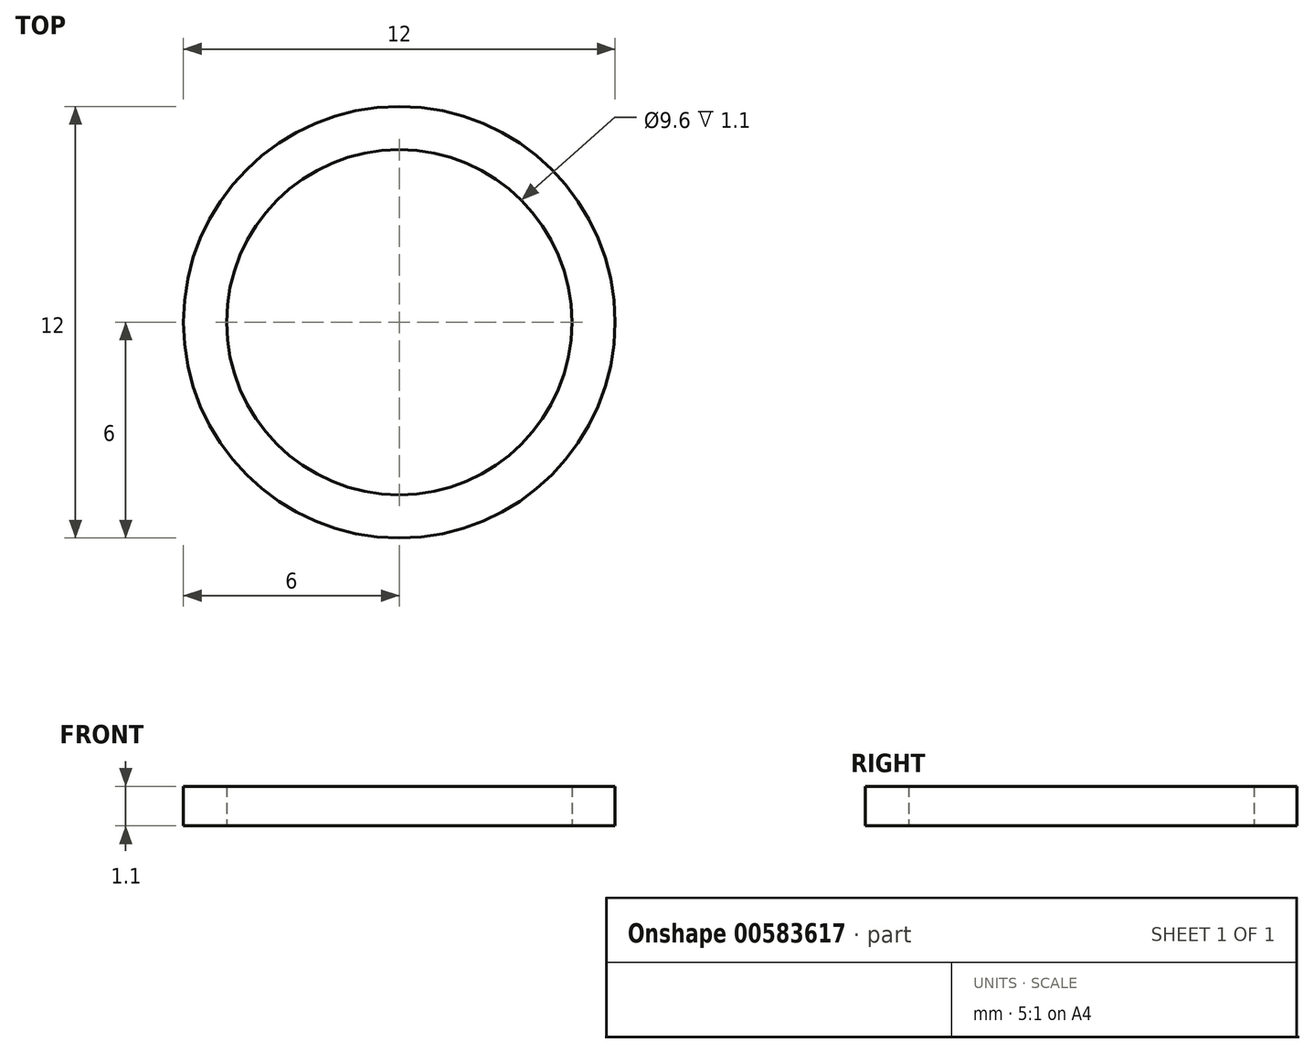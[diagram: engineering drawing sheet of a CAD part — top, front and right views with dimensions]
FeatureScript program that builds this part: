
annotation { "Feature Type Name" : "Feature", "Feature Type Description" : "" }
export const myFeature = defineFeature(function(context is Context, id is Id, definition is map)
    precondition{}
    {
        {
            var Q0;
            Q0=qCreatedBy(makeId("Top.planeOp"),FACE);
            var sketch = newSketch(context, id + "F0", { "sketchPlane" : qUnion([Q0])});
            skCircle(sketch, "E0", {"center": v(0, 0) * mm, "radius": 4.8 * mm});
            skCircle(sketch, "E1", {"center": v(0, 0) * mm, "radius": 6 * mm});
            skSolve(sketch);
        }
        {
            var Q0;
            Q0=makeQuery(id+"F0.imprint","IMPRINT",FACE,{"disambiguationData":[TD([[makeQuery(id+"F0.imprint","IMPRINT",EDGE,{"derivedFrom":sQuery(id+"F0.wireOp",EDGE,"E0")}),-1.0]])]});
            extrude(context, id + "F1", {"entities" : qUnion([Q0]), "depth" : 1.1 * mm, "offsetDistance" : 25.4 * mm});
        }
    });
